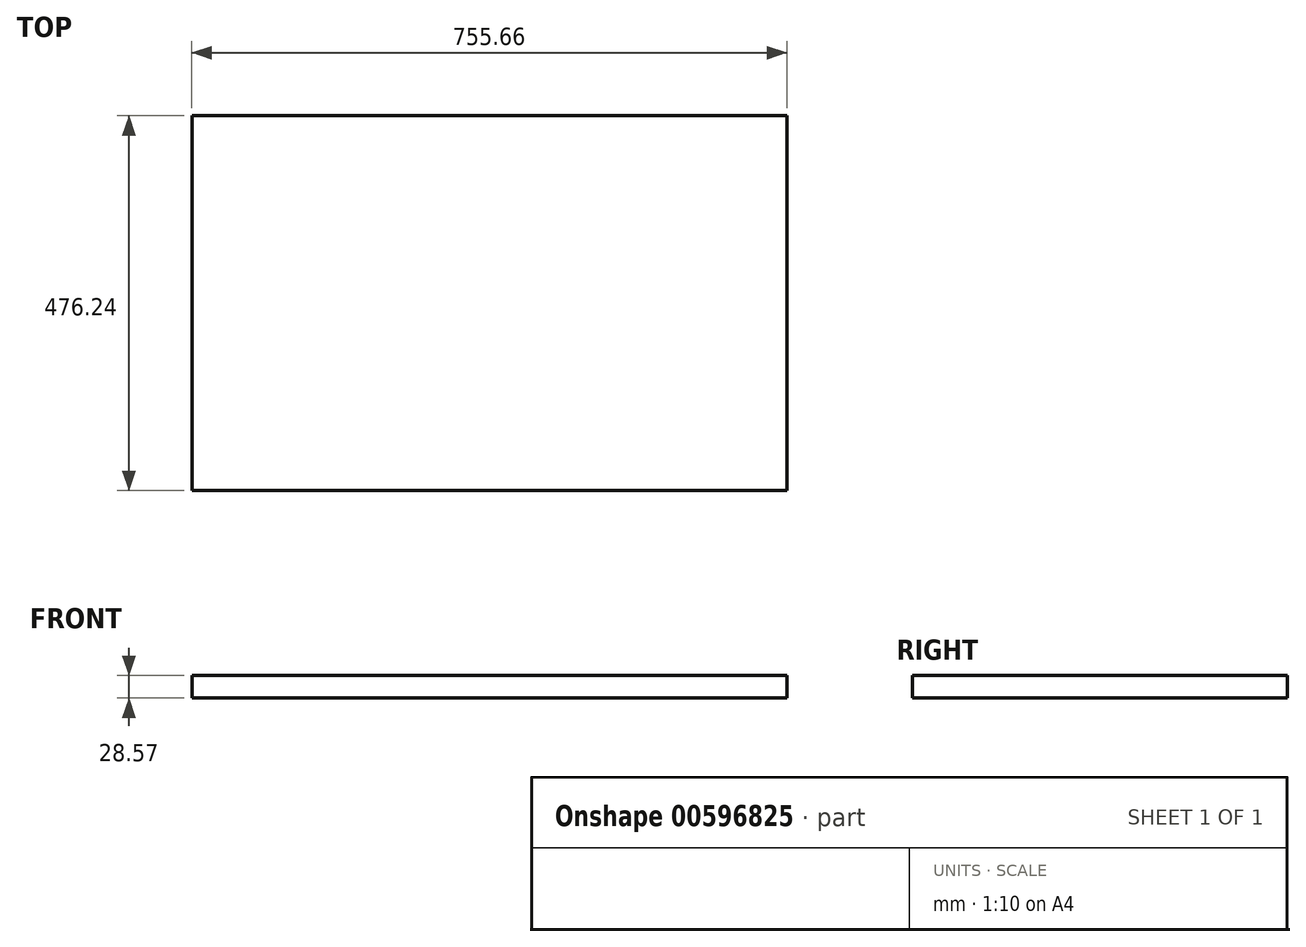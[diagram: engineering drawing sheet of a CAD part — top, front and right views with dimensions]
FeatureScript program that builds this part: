
annotation { "Feature Type Name" : "Feature", "Feature Type Description" : "" }
export const myFeature = defineFeature(function(context is Context, id is Id, definition is map)
    precondition{}
    {
        {
            var Q0;
            Q0=qCreatedBy(makeId("Top.planeOp"),FACE);
            var sketch = newSketch(context, id + "F0", { "sketchPlane" : qUnion([Q0])});
            skLineSegment(sketch, "E0.bottom", {"start": v(377.83, 238.13) * mm, "end": v(-377.83, 238.13) * mm});
            skLineSegment(sketch, "E0.top", {"start": v(377.83, -238.13) * mm, "end": v(-377.83, -238.13) * mm});
            skLineSegment(sketch, "E0.left", {"start": v(377.83, 238.13) * mm, "end": v(377.83, -238.13) * mm});
            skLineSegment(sketch, "E0.right", {"start": v(-377.83, 238.13) * mm, "end": v(-377.83, -238.13) * mm});
            skPoint(sketch, "E0.middle", {"position": v(0, 0) * mm});
            skSolve(sketch);
        }
        {
            var Q0;
            Q0=makeQuery(id+"F0.imprint","IMPRINT",FACE,{"disambiguationData":[TD([[makeQuery(id+"F0.imprint","IMPRINT",EDGE,{"derivedFrom":sQuery(id+"F0.wireOp",EDGE,"E0.bottom")}),1.0]])]});
            extrude(context, id + "F1", {"entities" : qUnion([Q0]), "depth" : 28.57 * mm, "offsetDistance" : 25.4 * mm});
        }
    });
